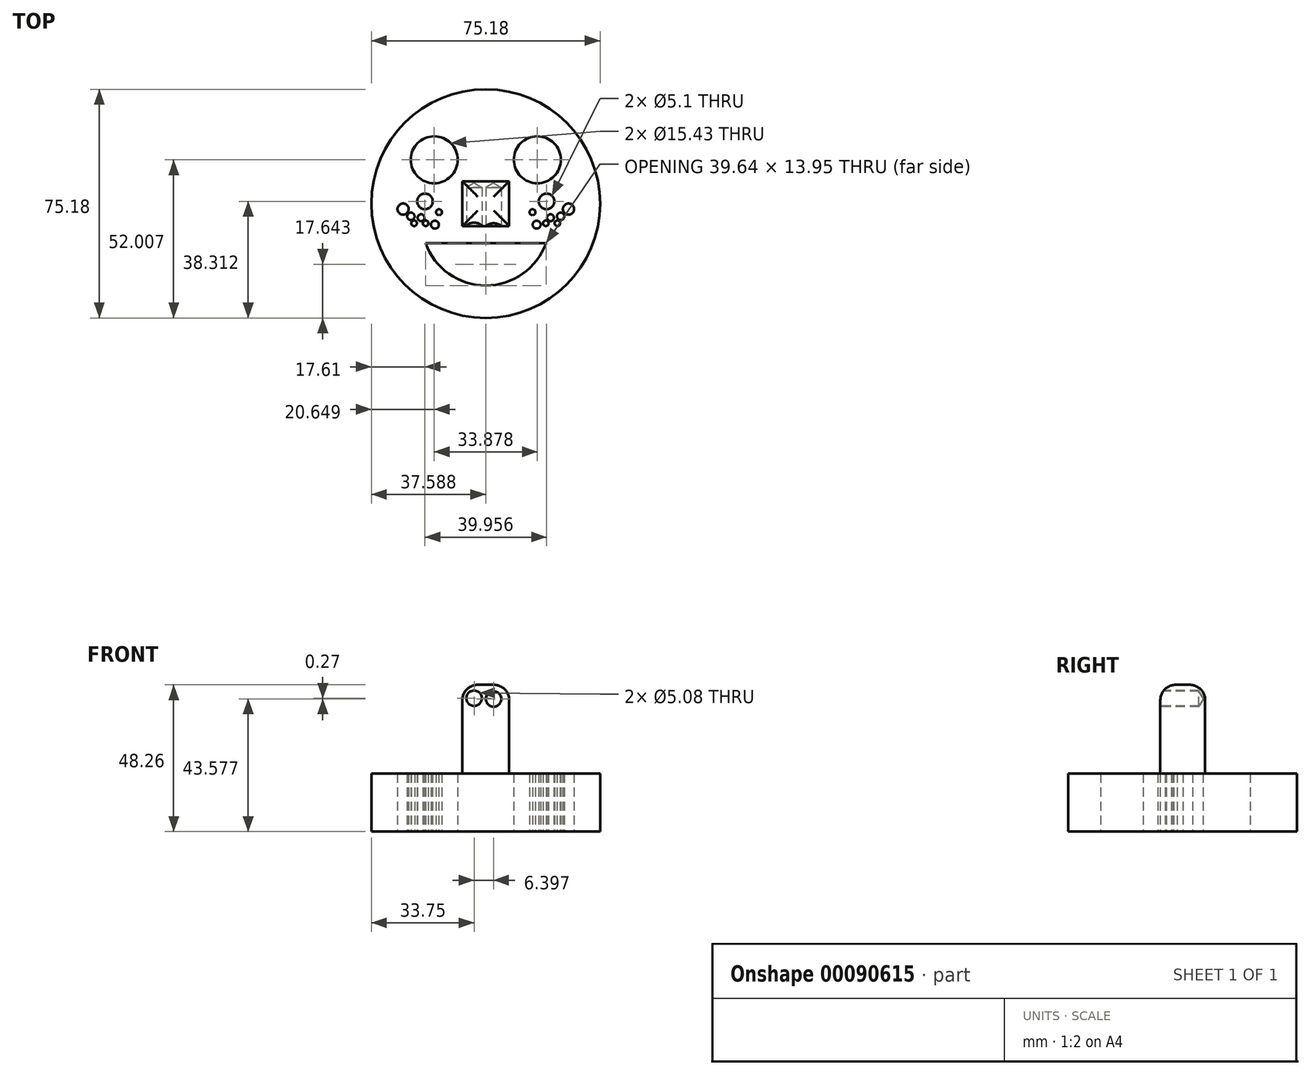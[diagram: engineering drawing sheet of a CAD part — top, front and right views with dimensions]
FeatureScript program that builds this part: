
annotation { "Feature Type Name" : "Feature", "Feature Type Description" : "" }
export const myFeature = defineFeature(function(context is Context, id is Id, definition is map)
    precondition{}
    {
        {
            var Q0;
            Q0=qCreatedBy(makeId("Top.planeOp"),FACE);
            var sketch = newSketch(context, id + "F0", { "sketchPlane" : qUnion([Q0])});
            skCircle(sketch, "E0", {"center": v(-46.13, 27.4) * mm, "radius": 37.59 * mm});
            skCircle(sketch, "E1", {"center": v(-63.07, 41.8) * mm, "radius": 7.71 * mm});
            skCircle(sketch, "E2.MirrorC", {"center": v(-29.2, 41.8) * mm, "radius": 7.71 * mm});
            skLineSegment(sketch, "E3", {"start": v(-46.13, 14.42) * mm, "end": v(-65.95, 14.42) * mm});
            skLineSegment(sketch, "E4.MirrorCS", {"start": v(-46.13, 14.42) * mm, "end": v(-26.3, 14.42) * mm});
            skArc(sketch, "E5", {"start": v(-65.95, 14.42) * mm, "mid": v(-46.13, 0.47) * mm, "end": v(-26.3, 14.42) * mm});
            skLineSegment(sketch, "E6.bottom", {"start": v(-38.42, 34.77) * mm, "end": v(-53.84, 34.77) * mm});
            skLineSegment(sketch, "E6.top", {"start": v(-38.42, 20.02) * mm, "end": v(-53.84, 20.02) * mm});
            skLineSegment(sketch, "E6.left", {"start": v(-38.42, 34.77) * mm, "end": v(-38.42, 20.02) * mm});
            skLineSegment(sketch, "E6.right", {"start": v(-53.84, 34.77) * mm, "end": v(-53.84, 20.02) * mm});
            skLineSegment(sketch, "E7", {"start": v(-46.13, 27.4) * mm, "end": v(-46.13, 64.98) * mm});
            skLineSegment(sketch, "E8", {"start": v(-46.13, 64.98) * mm, "end": v(-46.13, -10.2) * mm});
            skCircle(sketch, "E9", {"center": v(-73.32, 25.59) * mm, "radius": 1.84 * mm});
            skCircle(sketch, "E10", {"center": v(-66.1, 28.11) * mm, "radius": 2.55 * mm});
            skCircle(sketch, "E11", {"center": v(-61.5, 24.57) * mm, "radius": 0.97 * mm});
            skCircle(sketch, "E12", {"center": v(-65.89, 20.93) * mm, "radius": 0.91 * mm});
            skCircle(sketch, "E13", {"center": v(-62.86, 20.47) * mm, "radius": 1.3 * mm});
            skCircle(sketch, "E14", {"center": v(-70.74, 23.2) * mm, "radius": 1.22 * mm});
            skCircle(sketch, "E15", {"center": v(-69.68, 20.93) * mm, "radius": 0.91 * mm});
            skCircle(sketch, "E16", {"center": v(-67.4, 22.75) * mm, "radius": 1.13 * mm});
            skCircle(sketch, "E17.MirrorC", {"center": v(-26.15, 28.11) * mm, "radius": 2.55 * mm});
            skCircle(sketch, "E18.MirrorC", {"center": v(-29.4, 20.47) * mm, "radius": 1.3 * mm});
            skCircle(sketch, "E19.MirrorC", {"center": v(-30.77, 24.57) * mm, "radius": 0.97 * mm});
            skCircle(sketch, "E20.MirrorC", {"center": v(-24.86, 22.75) * mm, "radius": 1.13 * mm});
            skCircle(sketch, "E21.MirrorC", {"center": v(-26.38, 20.93) * mm, "radius": 0.91 * mm});
            skCircle(sketch, "E22.MirrorC", {"center": v(-22.59, 20.93) * mm, "radius": 0.91 * mm});
            skCircle(sketch, "E23.MirrorC", {"center": v(-21.53, 23.2) * mm, "radius": 1.22 * mm});
            skCircle(sketch, "E24.MirrorC", {"center": v(-18.95, 25.59) * mm, "radius": 1.84 * mm});
            skSolve(sketch);
        }
        {
            var Q0;
            Q0=makeQuery(id+"F0.imprint","IMPRINT",FACE,{"disambiguationData":[TD([[makeQuery(id+"F0.imprint","IMPRINT",EDGE,{"derivedFrom":sQuery(id+"F0.wireOp",EDGE,"E0")}),1.0]])]});
            extrude(context, id + "F1", {"entities" : qUnion([Q0]), "depth" : 19.05 * mm});
        }
        {
            var Q0;
            Q0=makeQuery(id+"F0.imprint","IMPRINT",FACE,{"disambiguationData":[TD([[makeQuery(id+"F0.imprint","IMPRINT",EDGE,{"derivedFrom":sQuery(id+"F0.wireOp",EDGE,"E6.bottom")}),1.0]])]});
            extrude(context, id + "F2", {"entities" : qUnion([Q0]), "operationType" : NewBodyOperationType.ADD, "depth" : 48.26 * mm});
        }
        {
            var Q0;
            Q0=makeQuery(id+"F2.opExtrude","SWEPT_FACE",FACE,{"disambiguationData":[OSD([sQuery(id+"F0.wireOp",EDGE,"E6.top")])]});
            var sketch = newSketch(context, id + "F3", { "sketchPlane" : qUnion([Q0])});
            skPoint(sketch, "E25", {"position": v(-49.97, 43.85) * mm});
            skPoint(sketch, "E26", {"position": v(-43.57, 43.58) * mm});
            skSolve(sketch);
        }
        {
            var Q0;
            Q0=sQuery(id+"F3.wireOp",VERTEX,"E25");
            var Q1;
            Q1=sQuery(id+"F3.wireOp",VERTEX,"E26");
            var Q2;
            Q2=makeQuery(id+"F1.opExtrude","SWEPT_BODY",BODY,{"disambiguationData":[OSD([sQuery(id+"F0.wireOp",EDGE,"E0"),sQuery(id+"F0.wireOp",EDGE,"E1"),sQuery(id+"F0.wireOp",EDGE,"E2.MirrorC"),sQuery(id+"F0.wireOp",EDGE,"E3"),sQuery(id+"F0.wireOp",EDGE,"E4.MirrorCS"),sQuery(id+"F0.wireOp",EDGE,"E5"),sQuery(id+"F0.wireOp",EDGE,"E6.bottom"),sQuery(id+"F0.wireOp",EDGE,"E6.top"),sQuery(id+"F0.wireOp",EDGE,"E6.left"),sQuery(id+"F0.wireOp",EDGE,"E6.right")])]});
            hole(context, id + "F4", {"style" : HoleStyle.SIMPLE, "endStyle" : HoleEndStyle.BLIND, "holeDiameter" : 5.08 * mm, "holeDepth" : 12.7 * mm, "locations" : qUnion([Q0, Q1]), "scope" : qUnion([Q2])});
        }
        {
            var Q0;
            Q0=makeQuery(id+"F2.opExtrude","CAP_EDGE",EDGE,{"disambiguationData":[OSD([sQuery(id+"F0.wireOp",EDGE,"E6.bottom")])],"isStart":false});
            var Q1;
            Q1=makeQuery(id+"F2.opExtrude","CAP_EDGE",EDGE,{"disambiguationData":[OSD([sQuery(id+"F0.wireOp",EDGE,"E6.right")])],"isStart":false});
            var Q2;
            Q2=makeQuery(id+"F2.opExtrude","CAP_EDGE",EDGE,{"disambiguationData":[OSD([sQuery(id+"F0.wireOp",EDGE,"E6.left")])],"isStart":false});
            var Q3;
            Q3=makeQuery(id+"F2.opExtrude","CAP_EDGE",EDGE,{"disambiguationData":[OSD([sQuery(id+"F0.wireOp",EDGE,"E6.top")])],"isStart":false});
            fillet(context, id + "F5", {"entities" : qUnion([Q0, Q1, Q2, Q3]), "radius" : 5.08 * mm, "tangentPropagation" : true, "allowEdgeOverflow" : false});
        }
    });
